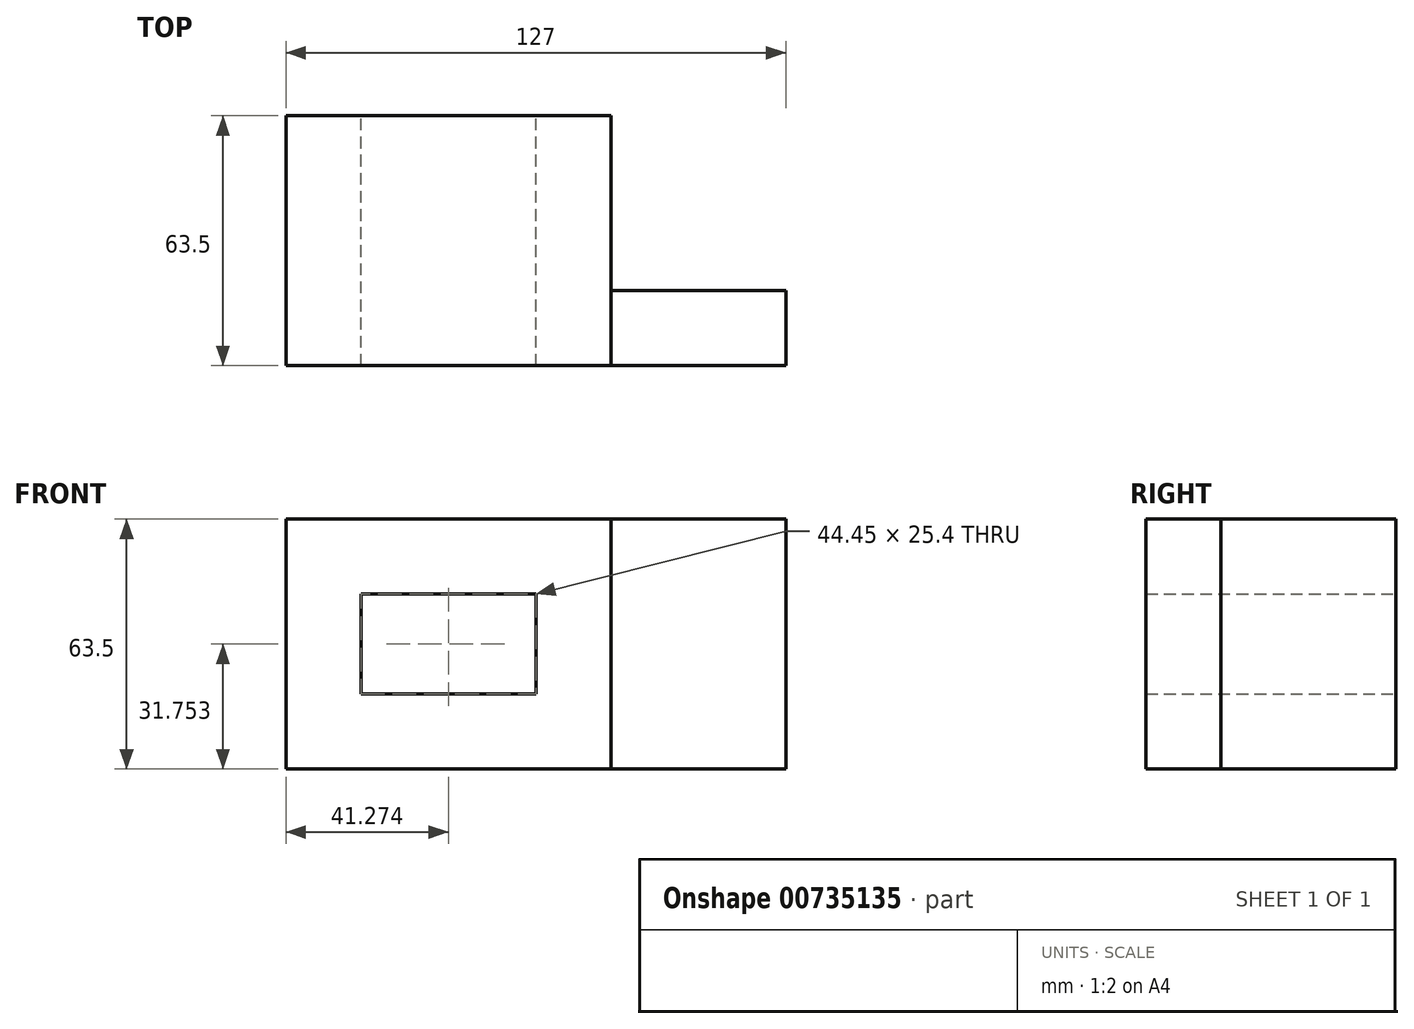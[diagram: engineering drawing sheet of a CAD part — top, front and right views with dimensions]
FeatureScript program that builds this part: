
annotation { "Feature Type Name" : "Feature", "Feature Type Description" : "" }
export const myFeature = defineFeature(function(context is Context, id is Id, definition is map)
    precondition{}
    {
        {
            var Q0;
            Q0=qCreatedBy(makeId("Front.planeOp"),FACE);
            var sketch = newSketch(context, id + "F0", { "sketchPlane" : qUnion([Q0])});
            skLineSegment(sketch, "E0.bottom", {"start": v(-23.32, 15.3) * mm, "end": v(21.13, 15.3) * mm});
            skLineSegment(sketch, "E0.top", {"start": v(-23.32, -10.1) * mm, "end": v(21.13, -10.1) * mm});
            skLineSegment(sketch, "E0.left", {"start": v(-23.32, 15.3) * mm, "end": v(-23.32, -10.1) * mm});
            skLineSegment(sketch, "E0.right", {"start": v(21.13, 15.3) * mm, "end": v(21.13, -10.1) * mm});
            skLineSegment(sketch, "E1.bottom", {"start": v(-42.37, 34.35) * mm, "end": v(40.18, 34.35) * mm});
            skLineSegment(sketch, "E1.top", {"start": v(-42.37, -29.15) * mm, "end": v(40.18, -29.15) * mm});
            skLineSegment(sketch, "E1.left", {"start": v(-42.37, 34.35) * mm, "end": v(-42.37, -29.15) * mm});
            skLineSegment(sketch, "E1.right", {"start": v(40.18, 34.35) * mm, "end": v(40.18, -29.15) * mm});
            skSolve(sketch);
        }
        {
            var Q0;
            Q0 = qSketchRegion(id + "F0", true);
            extrude(context, id + "F1", {"entities" : qUnion([Q0]), "depth" : 63.5 * mm, "offsetDistance" : 25.4 * mm});
        }
        {
            var Q0;
            Q0=makeQuery(id+"F1.opExtrude","CAP_FACE",FACE,{"disambiguationData":[OSD([sQuery(id+"F0.wireOp",EDGE,"E0.bottom"),sQuery(id+"F0.wireOp",EDGE,"E0.top"),sQuery(id+"F0.wireOp",EDGE,"E0.left"),sQuery(id+"F0.wireOp",EDGE,"E0.right"),sQuery(id+"F0.wireOp",EDGE,"E1.bottom"),sQuery(id+"F0.wireOp",EDGE,"E1.top"),sQuery(id+"F0.wireOp",EDGE,"E1.left"),sQuery(id+"F0.wireOp",EDGE,"E1.right")])],"isStart":false});
            var sketch = newSketch(context, id + "F2", { "sketchPlane" : qUnion([Q0])});
            skLineSegment(sketch, "E2", {"start": v(40.18, 34.35) * mm, "end": v(84.63, 34.35) * mm});
            skLineSegment(sketch, "E3", {"start": v(40.18, -29.15) * mm, "end": v(84.63, -29.15) * mm});
            skLineSegment(sketch, "E4", {"start": v(84.63, -29.15) * mm, "end": v(84.63, 34.35) * mm});
            skSolve(sketch);
        }
        {
            var Q0;
            Q0 = qSketchRegion(id + "F2", true);
            var Q1;
            Q1=makeQuery(id+"F2.imprint","IMPRINT",FACE,{"disambiguationData":[TD([[makeQuery(id+"F2.imprint","IMPRINT",EDGE,{"derivedFrom":sQuery(id+"F2.wireOp",EDGE,"E2")}),-1.0]])]});
            extrude(context, id + "F3", {"entities" : qUnion([Q0, Q1]), "oppositeDirection" : true, "depth" : 19.05 * mm, "offsetDistance" : 25.4 * mm});
        }
    });
